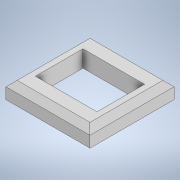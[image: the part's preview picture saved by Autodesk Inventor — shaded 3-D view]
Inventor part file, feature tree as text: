
AUTODESK INVENTOR PART (.ipt)
format: ipt  version: 2021 (Build 250183000, 183)  size: 105,984 bytes
history: native  units: in
note: dims shown in document units (in); Inventor stores cm internally (conversion verified against a paired STEP export)
features: extrude x1, chamfer x1, sketch x1
ambient origin geometry x8: Origin, YZ Plane, XZ Plane, XY Plane, X Axis, Y Axis, Z Axis, Center Point
bodies: Solid1 (feature_tree)
feature tree (3):
  extrude  "Extrusion1"  Depth=0.5906in
  chamfer  "Chamfer1"  Distance=0.2165in
  sketch  "Sketch1"  dims[d0=0.5906in d1=0.5906in d5=0.2165in d6=0.3346in d7=0.4331in d8=0.1181in d9=0.0in d10=0.0394in d11=0.0787in d12=45.0deg]
